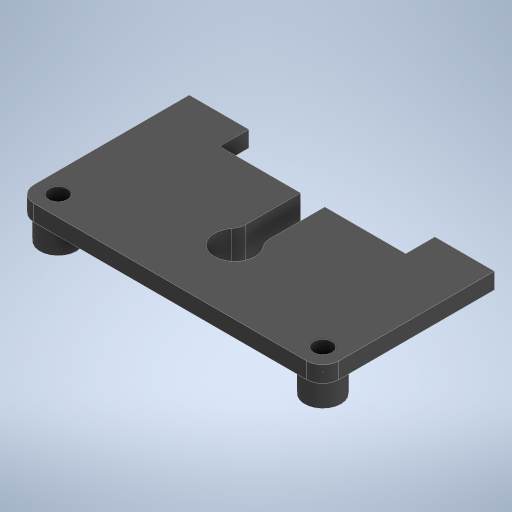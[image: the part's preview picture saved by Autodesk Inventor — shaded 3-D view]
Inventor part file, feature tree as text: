
AUTODESK INVENTOR PART (.ipt)
format: ipt  version: 2024.2 (Build 282272000, 272)  size: 389,632 bytes
history: native  units: mm
features: sketch x13, extrude x12, fillet x2
ambient origin geometry x8: Origin, YZ Plane, XZ Plane, XY Plane, X Axis, Y Axis, Z Axis, Center Point
bodies: Solid1 (feature_tree)
feature tree (27):
  extrude  "Extrusion1"  Depth=28.0mm
  extrude  "Extrusion2"  Depth=3.0mm
  extrude  "Extrusion3"  Depth=4.0mm
  extrude  "Extrusion4"  Depth=3.0mm TaperAngle=0.0deg
  fillet  "Fillet1"  Radius=48.2mm
  extrude  "Extrusion6"  Depth=4.85mm
  extrude  "Extrusion9"  Depth=2.0mm TaperAngle=0.0deg
  extrude  "Extrusion11"  Depth=2.35mm
  extrude  "Extrusion12"  Depth=4.5mm
  extrude  "Extrusion13"  Depth=2.35mm
  fillet  "Fillet3"  Radius=4.5mm
  sketch  "Sketch12"  dims[d27=2.35mm d28=4.5mm]
  extrude  "Extrusion14"  Depth=4.5mm
  extrude  "Extrusion16"  Depth=2.35mm
  extrude  "Extrusion17"  Depth=3.0mm TaperAngle=0.0deg
  sketch  "Sketch1"  dims[d0=28.0mm d1=38.5mm]
  sketch  "Sketch2"  dims[d6=3.0mm d7=0.0mm d8=4.0mm]
  sketch  "Sketch3"  dims[d9=4.0mm d10=4.0mm]
  sketch  "Sketch4"  dims[d11=4.0mm d12=3.0mm d13=0.0mm d14=48.2mm]
  sketch  "Sketch5"  dims[d15=37.7mm d16=4.85mm]
  sketch  "Sketch8"  dims[d17=4.85mm d18=2.0mm d19=0.0mm]
  sketch  "Sketch9"  dims[d20=4.5mm d21=2.35mm]
  sketch  "Sketch10"  dims[d22=2.35mm d23=4.5mm]
  sketch  "Sketch11"  dims[d24=2.35mm d25=2.35mm d26=4.5mm]
  sketch  "Sketch13"  dims[d29=2.35mm d30=2.35mm]
  sketch  "Sketch15"  dims[d31=2.35mm d32=3.0mm d33=0.0mm]
  sketch  "Sketch16"  dims[d34=2.0mm d45=2.0mm d46=2.0mm d51=0.0mm d52=0.0mm d68=5.0mm d69=3.125mm d70=18.85mm d71=0.0mm d72=0.0mm d73=28.0mm d76=3.0mm d77=1.5mm d81=24.1mm d82=4.85mm d83=23.0mm d84=13.0mm d85=7.35mm d86=6.5mm d87=0.0mm d88=0.0mm d90=0.0mm d91=0.0mm d93=0.0mm d94=0.0mm d95=2.0mm d96=2.3mm d97=2.3mm d98=0.0mm d99=0.0mm d107=4.0mm d108=0.0mm d109=2.5mm d110=2.5mm d111=0.4mm d112=0.0mm d113=0.0mm d63=0.5mm d64=0.872665mm d65=0.5mm d66=0.872665mm]
